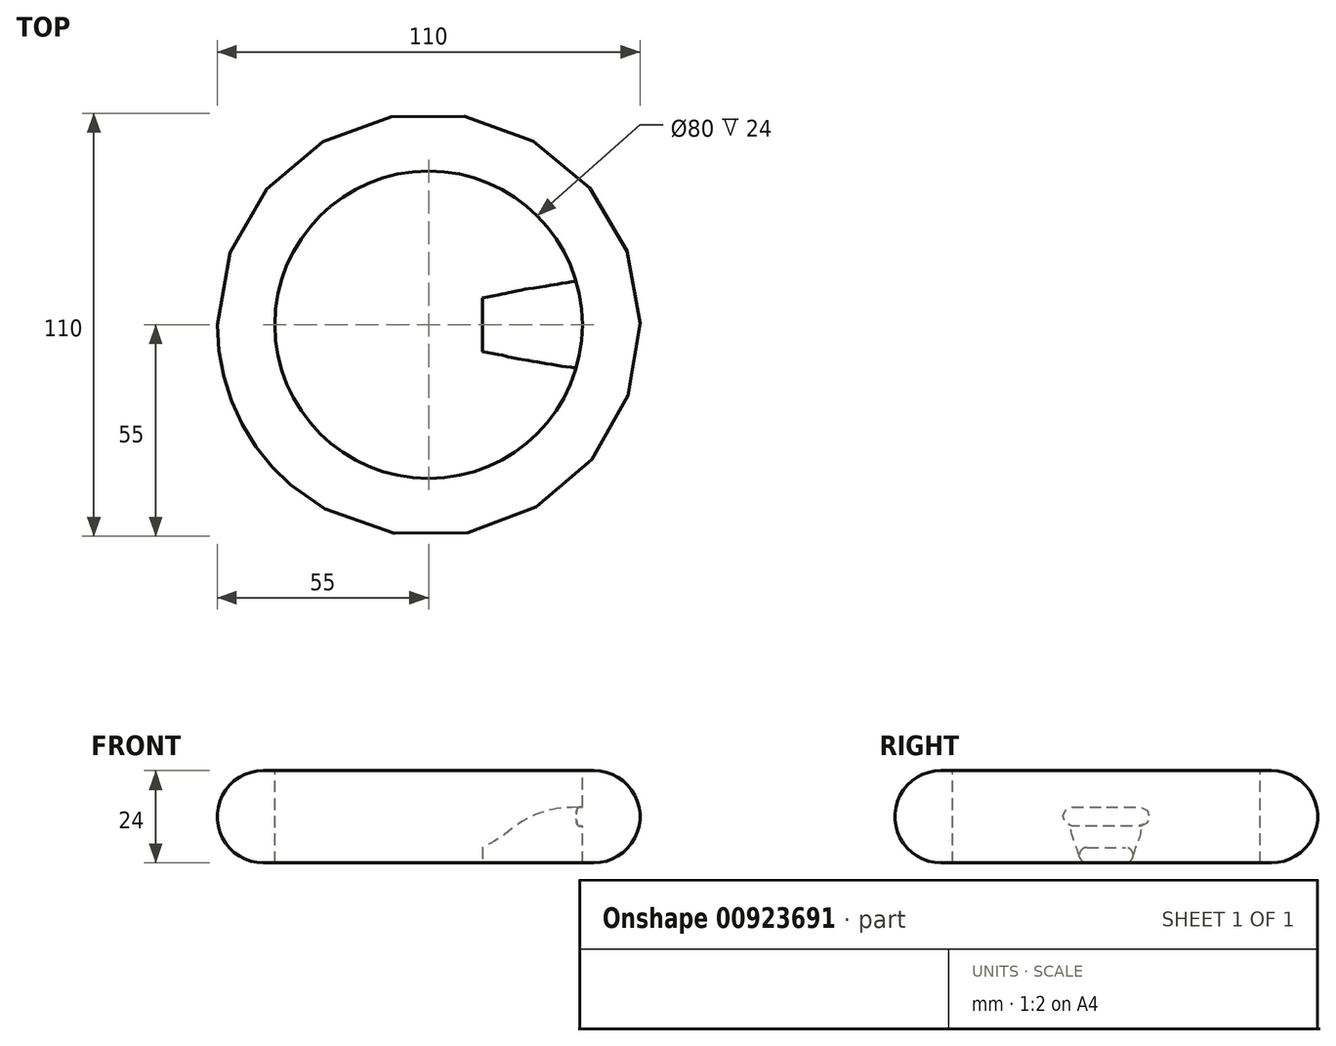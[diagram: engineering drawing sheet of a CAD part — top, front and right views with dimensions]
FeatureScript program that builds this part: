
annotation { "Feature Type Name" : "Feature", "Feature Type Description" : "" }
export const myFeature = defineFeature(function(context is Context, id is Id, definition is map)
    precondition{}
    {
        {
            var Q0;
            Q0=qCreatedBy(makeId("Top.planeOp"),FACE);
            var sketch = newSketch(context, id + "F0", { "sketchPlane" : qUnion([Q0])});
            skCircle(sketch, "E0", {"center": v(0, 0) * mm, "radius": 40 * mm});
            skSolve(sketch);
        }
        {
            var Q0;
            Q0=qCreatedBy(makeId("Front.planeOp"),FACE);
            var sketch = newSketch(context, id + "F1", { "sketchPlane" : qUnion([Q0])});
            skArc(sketch, "E1", {"start": v(-43, 12) * mm, "mid": v(-55, 0) * mm, "end": v(-43, -12) * mm});
            skLineSegment(sketch, "E2", {"start": v(-43, 12) * mm, "end": v(-40, 12) * mm});
            skLineSegment(sketch, "E3", {"start": v(-43, -12) * mm, "end": v(-40, -12) * mm});
            skLineSegment(sketch, "E4", {"start": v(-40, 12) * mm, "end": v(-40, -12) * mm});
            skSolve(sketch);
        }
        {
            var Q0;
            Q0=makeQuery(id+"F1.imprint","IMPRINT",FACE,{"disambiguationData":[TD([[makeQuery(id+"F1.imprint","IMPRINT",EDGE,{"derivedFrom":sQuery(id+"F1.wireOp",EDGE,"E1")}),1.0]])]});
            var Q1;
            Q1=sQuery(id+"F0.wireOp",EDGE,"E0");
            sweep(context, id + "F2", {"profiles" : qUnion([Q0]), "path" : qUnion([Q1])});
        }
        {
            var Q0;
            Q0=qCreatedBy(makeId("Right.planeOp"),FACE);
            cPlane(context, id + "F3", {"entities" : qUnion([Q0]), "cplaneType" : CPlaneType.OFFSET, "offset" : 40 * mm, "width" : 150 * mm, "height" : 150 * mm});
        }
        {
            var Q0;
            Q0=qCreatedBy(id+"F3.planeOp",FACE);
            var sketch = newSketch(context, id + "F4", { "sketchPlane" : qUnion([Q0])});
            skLineSegment(sketch, "E5", {"start": v(-9, 0) * mm, "end": v(9, 0) * mm});
            skArc(sketch, "E6.0.startCap", {"start": v(-9, -2.5) * mm, "mid": v(-11.5, 0) * mm, "end": v(-9, 2.5) * mm});
            skArc(sketch, "E6.0.endCap", {"start": v(9, 2.5) * mm, "mid": v(11.5, 0) * mm, "end": v(9, -2.5) * mm});
            skLineSegment(sketch, "E6.0.left", {"start": v(-9, 2.5) * mm, "end": v(9, 2.5) * mm});
            skLineSegment(sketch, "E6.0.right", {"start": v(-9, -2.5) * mm, "end": v(9, -2.5) * mm});
            skSolve(sketch);
        }
        {
            var Q0;
            Q0=qCreatedBy(makeId("Right.planeOp"),FACE);
            cPlane(context, id + "F5", {"entities" : qUnion([Q0]), "cplaneType" : CPlaneType.OFFSET, "offset" : 14 * mm, "width" : 150 * mm, "height" : 150 * mm});
        }
        {
            var Q0;
            Q0=qCreatedBy(id+"F5.planeOp",FACE);
            var sketch = newSketch(context, id + "F6", { "sketchPlane" : qUnion([Q0])});
            skLineSegment(sketch, "E7", {"start": v(-5, -10) * mm, "end": v(5, -10) * mm});
            skArc(sketch, "E8.0.startCap", {"start": v(-5, -12) * mm, "mid": v(-7, -10) * mm, "end": v(-5, -8) * mm});
            skArc(sketch, "E8.0.endCap", {"start": v(5, -8) * mm, "mid": v(7, -10) * mm, "end": v(5, -12) * mm});
            skLineSegment(sketch, "E8.0.left", {"start": v(-5, -8) * mm, "end": v(5, -8) * mm});
            skLineSegment(sketch, "E8.0.right", {"start": v(-5, -12) * mm, "end": v(5, -12) * mm});
            skSolve(sketch);
        }
        {
            var Q0;
            Q0=qCreatedBy(makeId("Front.planeOp"),FACE);
            var sketch = newSketch(context, id + "F7", { "sketchPlane" : qUnion([Q0])});
            skFitSpline(sketch, "E9", {"points": [v(14, -12) * mm, v(17.85, -9.7) * mm, v(18.98, -9.34) * mm, v(22.24, -7.74) * mm, v(24.61, -5.96) * mm, v(27.28, -4.5) * mm, v(30.71, -3.13) * mm, v(34.67, -2.44) * mm, v(36.02, -2.3) * mm, v(36.59, -2.13) * mm, v(40, -2.5) * mm], "startDerivative": vector(75.03, 34.15) * mm, "endDerivative": vector(78.85, -17.27) * mm});
            skSolve(sketch);
        }
        {
            var Q0;
            Q0=qConstructionFilter(qBodyType(qCreatedBy(id+"F7",EDGE),BodyType.WIRE),ConstructionObject.NO);
            var Q2;
            Q2=qSketchRegion(id+"F4",true);
            var Q3;
            Q3=qSketchRegion(id+"F6",true);
            loft(context, id + "F8", {"operationType" : NewBodyOperationType.ADD, "addSections" : true, "spine" : qUnion([Q0]), "sectionCount" : 5, "sheetProfilesArray" : [{ "sheetProfileEntities" : qUnion([Q2]) }, { "sheetProfileEntities" : qUnion([Q3]) }]});
        }
    });
